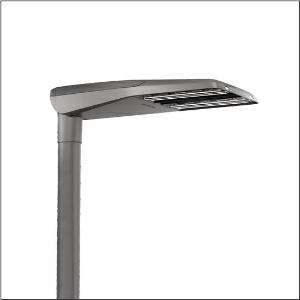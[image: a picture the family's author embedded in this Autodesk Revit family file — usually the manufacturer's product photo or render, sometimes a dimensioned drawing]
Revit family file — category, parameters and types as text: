
# Revit family: streetlight_sl_11_iq_midi___st1_2a_5xc3a61g08me_c756
name_source: partatom
category: Lighting Fixtures
units: mm (PartAtom-declared; Revit-internal decimal feet)

## family parameters
Cut with Voids When Loaded = No
Host = Face
Light Source = No
Part Type = Normal
Room Calculation Point = No
Round Connector Dimension = Use Diameter
Shared = No

## types (1)
- --- (1 x LED, 16120 lm, 123.9 W, 2700K)
    Apparent Load = 124 VA
    CIE Flux Codes = 32 70 96 100 100
    Color Rendering = 70
    Color Temperature = 2700K
    Default Elevation = 1800 mm
    Description = Streetlight SL 11 iQ midi, mast luminaire, primary light control with 3 zone facetted reflector, of plastic, silver coated, highly specular, primary optical cover: cover, of PMMA, transparent, light distribution: ST1.2a, light emission: direct distribution, primary light characteristic: asymmetric, installation type: post-top, side-entry, LED, High Power LED, rated luminous flux: 16.120lm, luminous efficacy: 130lm/W, light colour: 727, colour temperature: 2700K, control: Street-Remote, Auto-Match, Temp-Guard, Lumen-Switch, Night-Set, Smart-Wire, Light-Fading, Desk-Remote (wireless, voltage-free reading and setting of iQ features in the workshop via application-optimized NFC function/RFID function), optimised constant luminous flux control (CLO 2.0), presetting dimming linear, with cable H07RN-F 5x 1.5mm², mains connection: 230..240V, AC, 50/60Hz, connection cable pre-assembled, cable length: 12,5m, start of lifetime: 124W, end of service life: 131W, reduction: 57W, luminaire housing, of diecast aluminium, powder-coated, Siteco® metallic grey (DB 702S), please order mast flange separately, inclination adjustable without tools: 0°, 5°, 10°, 15° (post-top) | 0°, -5°, -10°, -15° (side-entry), sealing non-destructively replaceable, multi-level sealing system, length: 780mm, width: 376mm, height: 118mm, mast flange for spigot size: 42mm (side-entry): 5XC10008XM4, 60/48mm (side-entry/post-top): 5XC10108XM2, 76/60mm (side-entry/post-top): 5XC10108XM1, equipment: Power, protection rating (complete): IP66, insulation class (complete): insulation class II (safety insulation), certification: CE, ENEC, VDE, impact resistance: IK09, permissible operating ambient temperature for outdoor applications: -25..+50°C, standard-compliant lighting for roads and squares, Environmental Product Declaration (EPD) tested and certified by an independent institute, packaging unit: 1 piece

Light Distribution: ST1.2a
    Height = 118 mm
    Lamp = 1 x LED
    Lamp Light Flux = 16120 lm
    Lamp Power = 123.9 W
    Lamp count = 1
    Length = 780 mm
    Luminous efficacy = 130 lm/W
    Manufacturer = Siteco
    ModVariant = No
    Model = 5XC3A61G08ME
    Number of Poles = 1
    OnlyDefault = Yes
    Power Factor = 1
    Product Name = Streetlight SL 11 iQ midi | ST1.2a
    Product group = mast luminaire | pylon top
    ProductGroupID = 6100
    Protection Class = Protection class II
    Protection Degree = IP 66
    RLX_Detail_Level = 1
    RLX_Emergency_Light_Flux = 0 lm
    RLX_Emergency_Type = 0
    RLX_Emergency_Type_DB = No
    RlxData = <blob elided: 70873 chars, md5=bc0a42d4>
    Socket = socket
    Standby Power = 0 W
    System Light Flux = 16119 lm
    System Power = 124 W
    Type Comments = factory setting: luminous flux: 100 % | dim-lin: 254 | 554 mA
    Type Image = l_1005960.jpg
    URL = http://relux.com
    VarID = @adj_010461
    Voltage = 0 V
    Weight = 0.00 kg
    Width = 376 mm

## geometry (parser evidence)
native form markers: Blend x4, Sweep x11
no freeform markers — native parametric forms only
